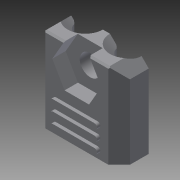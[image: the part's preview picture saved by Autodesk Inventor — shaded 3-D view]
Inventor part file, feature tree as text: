
AUTODESK INVENTOR PART (.ipt)
format: ipt  version: 2014 (Build 180170000, 170)  size: 207,360 bytes
history: native  units: in
note: dims shown in document units (in); Inventor stores cm internally (conversion verified against a paired STEP export)
features: extrude x6, sketch x6, chamfer x3, move_body x1, projected_geometry x1
ambient origin geometry x8: Origin, YZ Plane, XZ Plane, XY Plane, X Axis, Y Axis, Z Axis, Center Point
bodies: Solid1 (feature_tree)
feature tree (17):
  extrude  "Extrusion1"  Depth=0.7874in
  extrude  "Extrusion2"  Depth=0.2657in
  extrude  "Extrusion3"  Depth=0.1969in
  extrude  "Extrusion4"  Depth=0.2913in TaperAngle=0.0deg
  chamfer  "Chamfer1"  Distance=0.2913in
  chamfer  "Chamfer2"  Distance=0.195in
  chamfer  "Chamfer3"  Distance=0.2165in
  extrude  "Extrusion5"  Depth=0.03in
  extrude  "Extrusion6"  Depth=0.03in TaperAngle=0.0deg
  move_body  "Move Body1"
  sketch  "Sketch1"  dims[d0=0.7874in d1=0.7874in]
  sketch  "Sketch2"  dims[d2=0.2756in d3=0.0in d4=0.2657in]
  sketch  "Sketch3"  dims[d5=0.2657in d6=0.1969in]
  projected_geometry  "Projected Loop1"
  sketch  "Sketch4"  dims[d7=0.1969in d8=0.2913in d9=0.0in]
  sketch  "Sketch5"  dims[d10=0.1772in]
  sketch  "Sketch6"  dims[d11=0.1772in d12=0.2913in d13=0.0in d14=0.195in d15=0.2165in d16=0.1083in d17=0.2913in d18=0.0in d19=0.075in d20=0.125in d21=45.0deg d22=0.015in d23=0.125in d24=45.0deg d25=0.1in d26=0.125in d27=45.0deg d29=0.395in d30=0.125in d31=0.0in d32=0.3937in d33=0.05in d34=0.1in d35=0.1in d36=0.075in d37=1.1811in d39=0.1in d40=0.3937in d42=1.0in d44=0.03in d45=0.0in d46=270.0deg]
